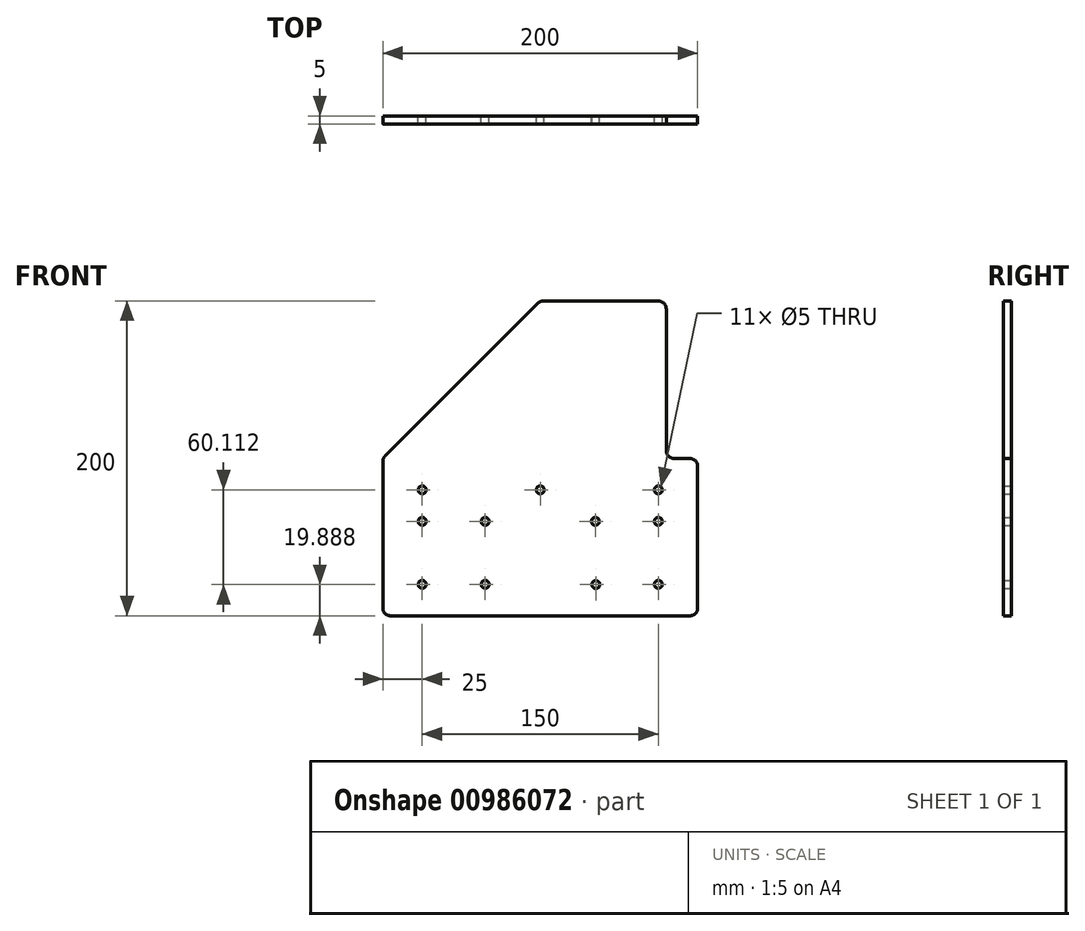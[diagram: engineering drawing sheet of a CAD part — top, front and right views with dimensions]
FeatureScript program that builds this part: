
annotation { "Feature Type Name" : "Feature", "Feature Type Description" : "" }
export const myFeature = defineFeature(function(context is Context, id is Id, definition is map)
    precondition{}
    {
        {
            var Q0;
            Q0=qCreatedBy(makeId("Front.planeOp"),FACE);
            var sketch = newSketch(context, id + "F0", { "sketchPlane" : qUnion([Q0])});
            skLineSegment(sketch, "E0", {"start": v(0, 5) * mm, "end": v(0, 97.93) * mm});
            skLineSegment(sketch, "E1", {"start": v(1.46, 101.46) * mm, "end": v(98.54, 198.54) * mm});
            skLineSegment(sketch, "E2", {"start": v(102.07, 200) * mm, "end": v(175, 200) * mm});
            skLineSegment(sketch, "E3", {"start": v(180, 195) * mm, "end": v(180, 105) * mm});
            skLineSegment(sketch, "E4", {"start": v(185, 100) * mm, "end": v(195, 100) * mm});
            skLineSegment(sketch, "E5", {"start": v(200, 95) * mm, "end": v(200, 5) * mm});
            skLineSegment(sketch, "E6", {"start": v(195, 0) * mm, "end": v(5, 0) * mm});
            skLineSegment(sketch, "E7", {"start": v(0, 20) * mm, "end": v(200, 20) * mm, "construction": true});
            skLineSegment(sketch, "E8", {"start": v(0, 60) * mm, "end": v(200, 60) * mm, "construction": true});
            skLineSegment(sketch, "E9", {"start": v(180, 120) * mm, "end": v(140, 120) * mm, "construction": true});
            skPoint(sketch, "E9.endSnap0", {"position": v(140, 200) * mm});
            skLineSegment(sketch, "E10", {"start": v(140, 120) * mm, "end": v(140, 200) * mm, "construction": true});
            skLineSegment(sketch, "E11", {"start": v(160, 140) * mm, "end": v(160, 180) * mm, "construction": true});
            skLineSegment(sketch, "E12", {"start": v(160, 140) * mm, "end": v(180, 140) * mm, "construction": true});
            skLineSegment(sketch, "E13", {"start": v(160, 180) * mm, "end": v(180, 180) * mm, "construction": true});
            skLineSegment(sketch, "E14", {"start": v(0, 80) * mm, "end": v(200, 80) * mm, "construction": true});
            skCircle(sketch, "E15", {"center": v(25, 60) * mm, "radius": 2.5 * mm});
            skCircle(sketch, "E16", {"center": v(25, 80) * mm, "radius": 2.5 * mm});
            skCircle(sketch, "E17", {"center": v(100, 80) * mm, "radius": 2.5 * mm});
            skCircle(sketch, "E18", {"center": v(65, 20) * mm, "radius": 2.5 * mm});
            skPoint(sketch, "E19.visualSharp", {"position": v(0, 100) * mm});
            skArc(sketch, "E19.filletArc", {"start": v(1.46, 101.46) * mm, "mid": v(0.38, 99.84) * mm, "end": v(0, 97.93) * mm});
            skPoint(sketch, "E20.visualSharp", {"position": v(0, 0) * mm});
            skArc(sketch, "E20.filletArc", {"start": v(0, 5) * mm, "mid": v(1.46, 1.46) * mm, "end": v(5, 0) * mm});
            skPoint(sketch, "E21.visualSharp", {"position": v(200, 0) * mm});
            skArc(sketch, "E21.filletArc", {"start": v(195, 0) * mm, "mid": v(198.54, 1.46) * mm, "end": v(200, 5) * mm});
            skPoint(sketch, "E22.visualSharp", {"position": v(200, 100) * mm});
            skArc(sketch, "E22.filletArc", {"start": v(200, 95) * mm, "mid": v(198.54, 98.54) * mm, "end": v(195, 100) * mm});
            skPoint(sketch, "E23.visualSharp", {"position": v(180, 100) * mm});
            skArc(sketch, "E23.filletArc", {"start": v(180, 105) * mm, "mid": v(181.46, 101.46) * mm, "end": v(185, 100) * mm});
            skPoint(sketch, "E24.visualSharp", {"position": v(100, 200) * mm});
            skArc(sketch, "E24.filletArc", {"start": v(102.07, 200) * mm, "mid": v(100.16, 199.62) * mm, "end": v(98.54, 198.54) * mm});
            skPoint(sketch, "E25.visualSharp", {"position": v(180, 200) * mm});
            skArc(sketch, "E25.filletArc", {"start": v(180, 195) * mm, "mid": v(178.54, 198.54) * mm, "end": v(175, 200) * mm});
            skCircle(sketch, "E26", {"center": v(65, 60) * mm, "radius": 2.5 * mm});
            skLineSegment(sketch, "E27", {"start": v(25, 91.63) * mm, "end": v(25, 8.17) * mm, "construction": true});
            skCircle(sketch, "E28", {"center": v(25, 20) * mm, "radius": 2.5 * mm});
            skLineSegment(sketch, "E29", {"start": v(65, 93.23) * mm, "end": v(65, 7.87) * mm, "construction": true});
            skLineSegment(sketch, "E30", {"start": v(175, 95.24) * mm, "end": v(175, 7.2) * mm, "construction": true});
            skCircle(sketch, "E31", {"center": v(175, 80) * mm, "radius": 2.5 * mm});
            skCircle(sketch, "E32", {"center": v(175, 60) * mm, "radius": 2.5 * mm});
            skCircle(sketch, "E33", {"center": v(175, 20) * mm, "radius": 2.5 * mm});
            skLineSegment(sketch, "E34", {"start": v(135, 94.59) * mm, "end": v(135, 10.55) * mm, "construction": true});
            skCircle(sketch, "E35", {"center": v(135, 60) * mm, "radius": 2.5 * mm});
            skCircle(sketch, "E36", {"center": v(135.28, 19.89) * mm, "radius": 2.5 * mm});
            skSolve(sketch);
        }
        {
            var Q0;
            Q0=makeQuery(id+"F0.imprint","IMPRINT",FACE,{"disambiguationData":[TD([[makeQuery(id+"F0.imprint","IMPRINT",EDGE,{"derivedFrom":sQuery(id+"F0.wireOp",EDGE,"E0")}),-1.0]])]});
            extrude(context, id + "F1", {"entities" : qUnion([Q0]), "depth" : 5 * mm, "offsetDistance" : 25 * mm});
        }
    });
